# Revit family: HubModulSofa
name_source: partatom
category: Furniture
units: mm (PartAtom-declared; Revit-internal decimal feet)

## family parameters
Always vertical = Yes
Cut with Voids When Loaded = No
OmniClass Number = 23.40.20.00
OmniClass Title = General Furniture and Specialties
Room Calculation Point = No
Shared = No
Work Plane-Based = No

## types (6) — shared parameters
Depth = 730 mm  [stored 2.39501 ft]
LegsHeight = 120 mm  [stored 0.393701 ft]
ManufactureURL = https://www.isku.com
Manufacturer = ISKU
Model = Hub Modul Sofa
SeatHeight = 460 mm  [stored 1.50919 ft]
zero-valued in all types: NorminalDepth, NorminalHeight

## per-type parameters (varying)
| type | CournerBackrest | Height | OverallWidth | SeatDepth | SmallCournerBackrest | StraightBackrest | Width |
| 730 x 730 | No | 460 mm  [stored 1.50919 ft] | 730 mm  [stored 2.39501 ft] | 730 mm  [stored 2.39501 ft] | No | No | 730 mm  [stored 2.39501 ft] |
| 1460 x 730 | No | 460 mm  [stored 1.50919 ft] | 1460 mm  [stored 4.79003 ft] | 730 mm  [stored 2.39501 ft] | No | No | 1460 mm  [stored 4.79003 ft] |
| 730 x 730 WithStraightBackrest | No | 800 mm  [stored 2.62467 ft] | 1460 mm  [stored 4.79003 ft] | 505 mm  [stored 1.65682 ft] | No | Yes | 730 mm  [stored 2.39501 ft] |
| 730 x 730 WithCournerBackrest | Yes | 800 mm  [stored 2.62467 ft] | 1460 mm  [stored 4.79003 ft] | 505 mm  [stored 1.65682 ft] | No | No | 730 mm  [stored 2.39501 ft] |
| 1460 x 730 WithStraightBackrest | No | 800 mm  [stored 2.62467 ft] | 2190 mm  [stored 7.18504 ft] | 505 mm  [stored 1.65682 ft] | No | Yes | 1460 mm  [stored 4.79003 ft] |
| 1460 x 730 WithSmallCournerBackrest | No | 800 mm  [stored 2.62467 ft] | 1460 mm  [stored 4.79003 ft] | 505 mm  [stored 1.65682 ft] | Yes | No | 1460 mm  [stored 4.79003 ft] |

note: [stored X ft] marks values corroborated as IEEE doubles in the binary element streams (Revit-internal decimal feet)

## geometry (parser evidence)
native form markers: Sweep x23
no freeform markers — native parametric forms only
